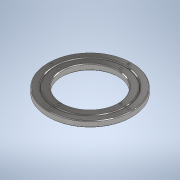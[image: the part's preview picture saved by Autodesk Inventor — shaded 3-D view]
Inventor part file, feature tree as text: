
AUTODESK INVENTOR PART (.ipt)
format: ipt  version: 2021 (Build 250183000, 183)  size: 193,536 bytes
history: native  units: mm
features: extrude x3, sketch x3, chamfer x2
ambient origin geometry x8: Origin, YZ Plane, XZ Plane, XY Plane, X Axis, Y Axis, Z Axis, Center Point
bodies: Solid1 (feature_tree)
feature tree (8):
  extrude  "Extrusion1"  Depth=100.0mm
  chamfer  "Chamfer1"  Distance=8.5mm
  chamfer  "Chamfer2"  Distance=1.0mm Angle=45.0deg
  extrude  "Extrusion2"  Depth=8.5mm TaperAngle=45.0deg
  extrude  "Extrusion3"  Depth=8.5mm
  sketch  "Sketch1"  dims[d0=79.8mm d1=100.0mm]
  sketch  "Sketch2"  dims[d2=120.0mm]
  sketch  "Sketch3"  dims[d3=101.0mm d4=8.5mm d5=0.0mm d6=1.0mm d7=2.0mm d8=45.0deg d9=1.0mm d10=2.0mm d11=45.0deg d12=3.2mm d13=3.2mm d14=3.2mm d15=3.2mm d16=77.782mm d17=77.782mm d18=77.782mm d19=77.782mm d20=0.0mm d21=0.0mm d22=0.0mm d23=8.5mm d24=0.0mm d25=55.0mm d26=3.2mm d27=3.2mm d28=3.2mm d29=3.2mm d30=62.225mm d31=62.225mm d32=62.225mm d33=62.225mm d34=44.0mm d35=44.0mm d36=44.0mm d37=8.5mm d38=0.0mm]
